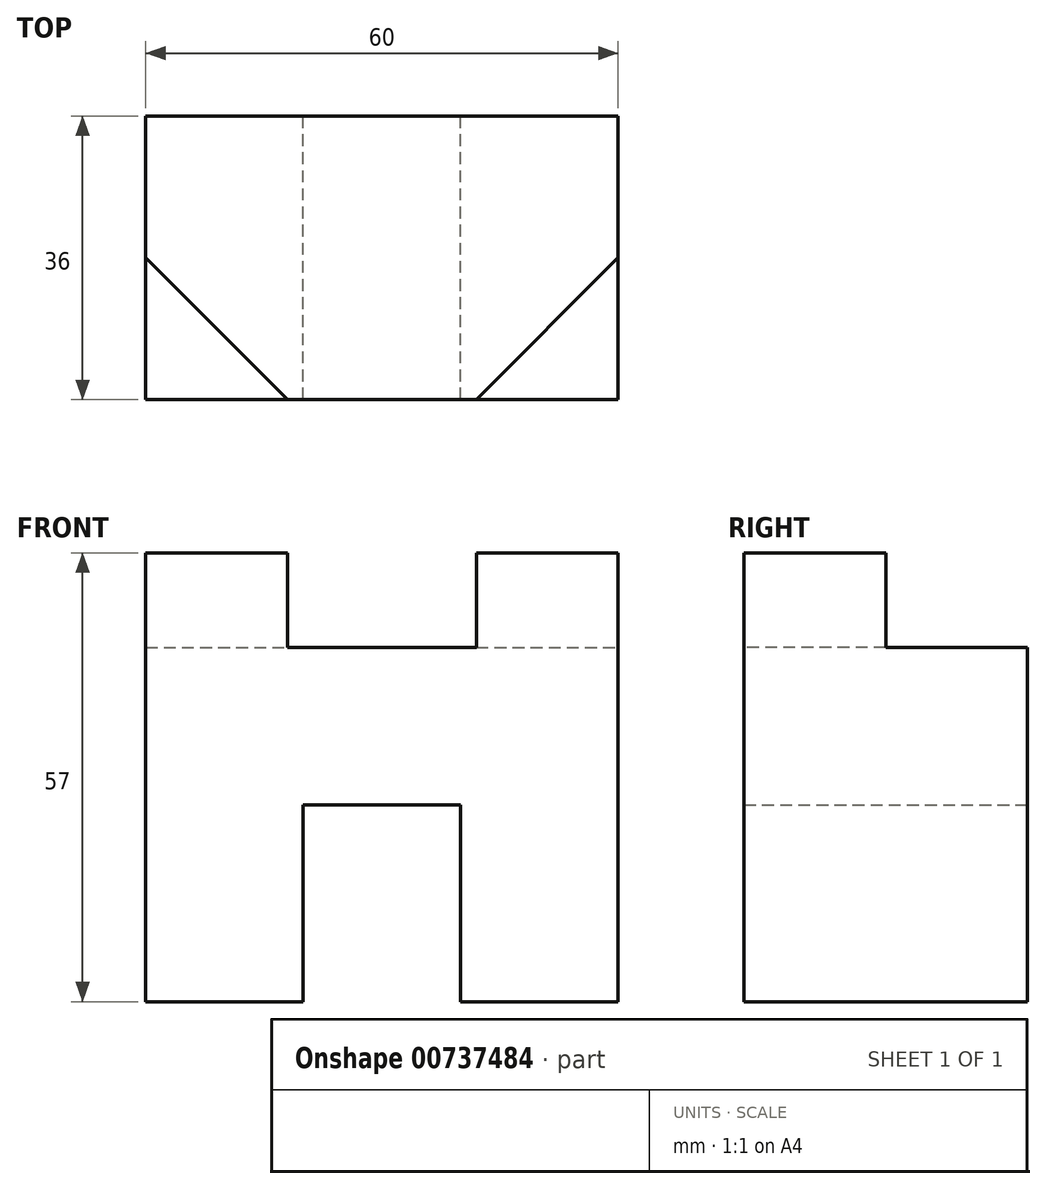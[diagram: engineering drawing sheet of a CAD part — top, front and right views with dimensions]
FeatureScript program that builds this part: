
annotation { "Feature Type Name" : "Feature", "Feature Type Description" : "" }
export const myFeature = defineFeature(function(context is Context, id is Id, definition is map)
    precondition{}
    {
        {
            var Q0;
            Q0=qCreatedBy(makeId("Front.planeOp"),FACE);
            var sketch = newSketch(context, id + "F0", { "sketchPlane" : qUnion([Q0])});
            skLineSegment(sketch, "E0.bottom", {"start": v(30, 22.5) * mm, "end": v(-30, 22.5) * mm});
            skLineSegment(sketch, "E0.top", {"start": v(30, -22.5) * mm, "end": v(10, -22.5) * mm});
            skLineSegment(sketch, "E0.left", {"start": v(30, 22.5) * mm, "end": v(30, -22.5) * mm});
            skLineSegment(sketch, "E0.right", {"start": v(-30, 22.5) * mm, "end": v(-30, -22.5) * mm});
            skPoint(sketch, "E0.middle", {"position": v(0, 0) * mm});
            skLineSegment(sketch, "E1", {"start": v(-30, 22.5) * mm, "end": v(-10, 22.5) * mm});
            skLineSegment(sketch, "E2", {"start": v(30, 22.5) * mm, "end": v(10, 22.5) * mm});
            skLineSegment(sketch, "E3", {"start": v(-10, 22.5) * mm, "end": v(-10, 34.5) * mm});
            skLineSegment(sketch, "E4", {"start": v(-10, 34.5) * mm, "end": v(-30, 34.5) * mm});
            skLineSegment(sketch, "E5", {"start": v(-30, 22.5) * mm, "end": v(-30, 34.5) * mm});
            skLineSegment(sketch, "E6", {"start": v(10, 22.5) * mm, "end": v(10, 34.5) * mm});
            skLineSegment(sketch, "E7", {"start": v(30, 22.5) * mm, "end": v(30, 34.5) * mm});
            skLineSegment(sketch, "E8", {"start": v(10, 34.5) * mm, "end": v(30, 34.5) * mm});
            skLineSegment(sketch, "E9", {"start": v(-30, -22.5) * mm, "end": v(-10, -22.5) * mm});
            skLineSegment(sketch, "E10", {"start": v(-10, -22.5) * mm, "end": v(-10, 2.5) * mm});
            skLineSegment(sketch, "E11", {"start": v(10, -22.5) * mm, "end": v(10, 2.5) * mm});
            skLineSegment(sketch, "E12", {"start": v(-10, 2.5) * mm, "end": v(10, 2.5) * mm});
            skLineSegment(sketch, "E13.trimOffspring", {"start": v(-10, -22.5) * mm, "end": v(-30, -22.5) * mm});
            skSolve(sketch);
        }
        {
            var Q0;
            Q0=makeQuery(id+"F0.imprint","IMPRINT",FACE,{"disambiguationData":[TD([[makeQuery(id+"F0.imprint","IMPRINT",EDGE,{"derivedFrom":sQuery(id+"F0.wireOp",EDGE,"E0.bottom")}),1.0]])]});
            extrude(context, id + "F1", {"entities" : qUnion([Q0]), "depth" : 36 * mm, "offsetDistance" : 25 * mm});
        }
        {
            var Q0;
            Q0=makeQuery(id+"F1.opExtrude","SWEPT_FACE",FACE,{"disambiguationData":[OSD([sQuery(id+"F0.wireOp",EDGE,"E0.bottom"),sQuery(id+"F0.wireOp",EDGE,"E1"),sQuery(id+"F0.wireOp",EDGE,"E2")])]});
            var sketch = newSketch(context, id + "F2", { "sketchPlane" : qUnion([Q0])});
            skLineSegment(sketch, "E14", {"start": v(-30, -36) * mm, "end": v(30, -36) * mm});
            skLineSegment(sketch, "E15", {"start": v(-30, -36) * mm, "end": v(-30, -18) * mm});
            skLineSegment(sketch, "E16", {"start": v(30, -36) * mm, "end": v(30, -18) * mm});
            skLineSegment(sketch, "E17", {"start": v(-30, -36) * mm, "end": v(-12, -36) * mm});
            skLineSegment(sketch, "E18", {"start": v(30, -36) * mm, "end": v(12, -36) * mm});
            skLineSegment(sketch, "E19", {"start": v(-30, -18) * mm, "end": v(-12, -36) * mm});
            skLineSegment(sketch, "E20", {"start": v(12, -36) * mm, "end": v(30, -18) * mm});
            skSolve(sketch);
        }
        {
            var Q0;
            Q0=makeQuery(id+"F2.imprint","IMPRINT",FACE,{"disambiguationData":[TD([[makeQuery(id+"F2.imprint","IMPRINT",EDGE,{"derivedFrom":sQuery(id+"F2.wireOp",EDGE,"E15")}),-1.0]])]});
            var Q1;
            Q1=makeQuery(id+"F2.imprint","IMPRINT",FACE,{"disambiguationData":[TD([[makeQuery(id+"F2.imprint","IMPRINT",EDGE,{"derivedFrom":sQuery(id+"F2.wireOp",EDGE,"E16")}),1.0]])]});
            extrude(context, id + "F3", {"entities" : qUnion([Q0, Q1]), "operationType" : NewBodyOperationType.ADD, "depth" : 12 * mm, "offsetDistance" : 25 * mm});
        }
    });
